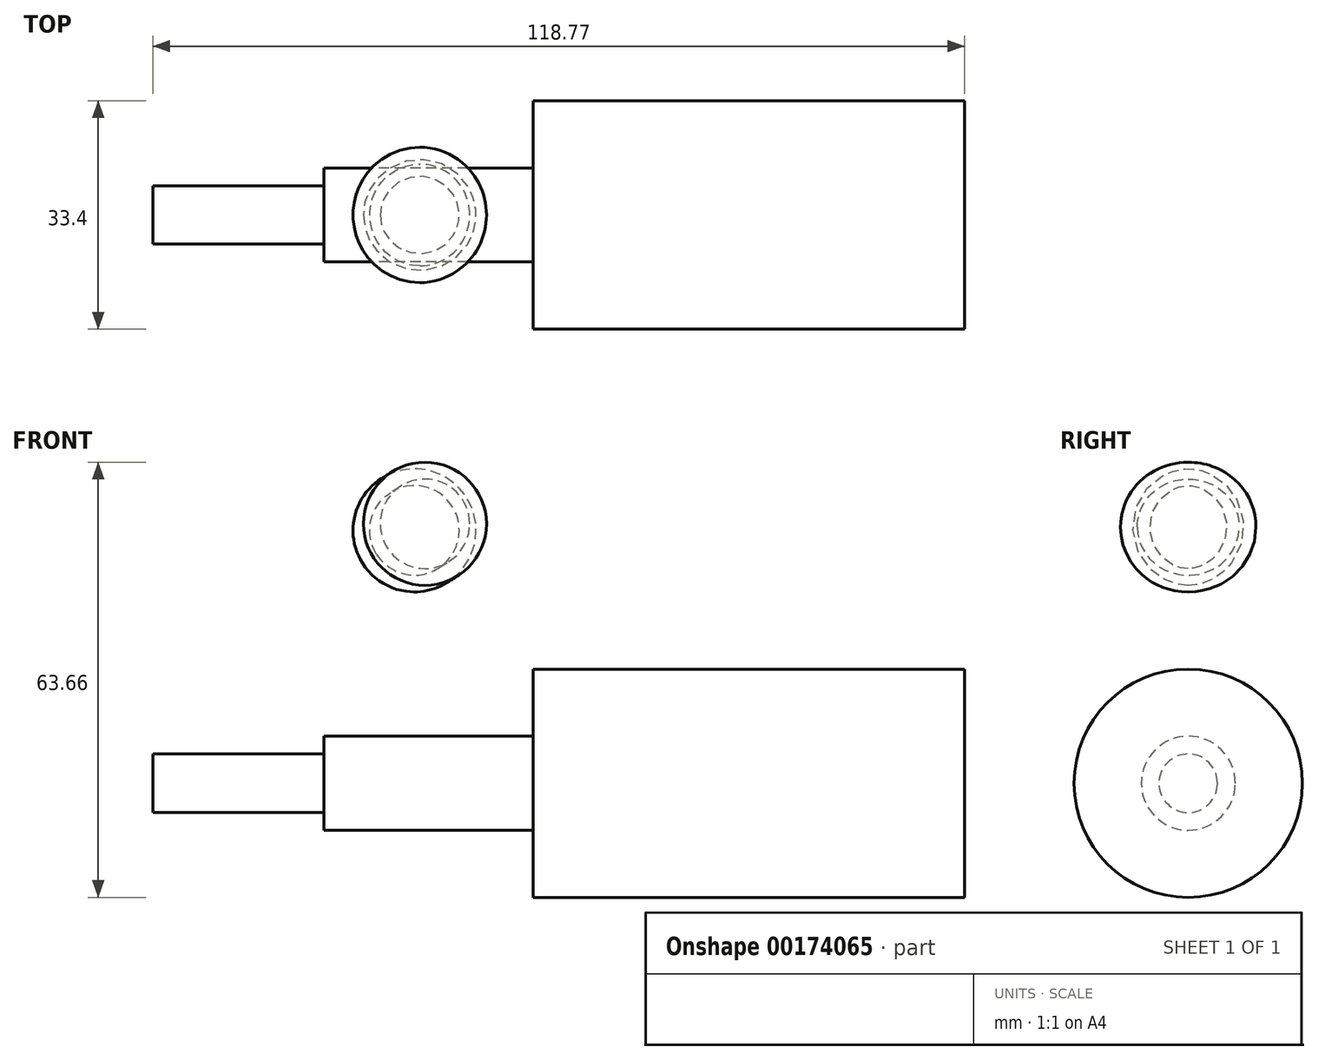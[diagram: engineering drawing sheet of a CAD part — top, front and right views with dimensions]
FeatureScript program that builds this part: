
annotation { "Feature Type Name" : "Feature", "Feature Type Description" : "" }
export const myFeature = defineFeature(function(context is Context, id is Id, definition is map)
    precondition{}
    {
        {
            var Q0;
            Q0=qCreatedBy(makeId("Front.planeOp"),FACE);
            var sketch = newSketch(context, id + "F0", { "sketchPlane" : qUnion([Q0])});
            skLineSegment(sketch, "E0", {"start": v(-42.95, -6.88) * mm, "end": v(-12.35, -6.88) * mm});
            skLineSegment(sketch, "E1", {"start": v(-12.35, -6.88) * mm, "end": v(-12.35, -16.7) * mm});
            skLineSegment(sketch, "E2", {"start": v(-12.35, -16.7) * mm, "end": v(50.82, -16.7) * mm});
            skLineSegment(sketch, "E3", {"start": v(50.82, -16.7) * mm, "end": v(50.82, 0) * mm});
            skLineSegment(sketch, "E4", {"start": v(-42.95, 0) * mm, "end": v(50.82, 0) * mm});
            skLineSegment(sketch, "E5", {"start": v(-42.95, 0) * mm, "end": v(-42.95, -6.88) * mm});
            skSolve(sketch);
        }
        {
            var Q0;
            Q0=makeQuery(id+"F0.imprint","IMPRINT",FACE,{"disambiguationData":[TD([[makeQuery(id+"F0.imprint","IMPRINT",EDGE,{"derivedFrom":sQuery(id+"F0.wireOp",EDGE,"E0")}),1.0]])]});
            var Q1;
            Q1=sQuery(id+"F0.wireOp",EDGE,"E4");
            revolve(context, id + "F1", {"entities" : qUnion([Q0]), "axis" : qUnion([Q1]), "revolveType" : RevolveType.FULL});
        }
        {
            var Q0;
            Q0=qCreatedBy(makeId("Front.planeOp"),FACE);
            var sketch = newSketch(context, id + "F2", { "sketchPlane" : qUnion([Q0])});
            skArc(sketch, "E6", {"start": v(-24.14, 29.9) * mm, "mid": v(-22.06, 41.8) * mm, "end": v(-33.69, 45.06) * mm});
            skLineSegment(sketch, "E7", {"start": v(-33.69, 45.06) * mm, "end": v(-24.14, 29.9) * mm});
            skArc(sketch, "E8", {"start": v(-25.46, 32) * mm, "mid": v(-24.14, 40.49) * mm, "end": v(-32.37, 42.97) * mm});
            skSolve(sketch);
        }
        {
            var Q0;
            {var subQ0=sQuery(id+"F2.wireOp",EDGE,"E6");Q0=makeQuery(id+"F2.imprint","IMPRINT",FACE,{"disambiguationData":[TD([[makeQuery(id+"F2.imprint","IMPRINT",EDGE,{"derivedFrom":subQ0}),1.0]])]});}
            var Q1;
            Q1=sQuery(id+"F2.wireOp",EDGE,"E7");
            revolve(context, id + "F3", {"entities" : qUnion([Q0]), "axis" : qUnion([Q1]), "revolveType" : RevolveType.FULL});
        }
        {
            var Q0;
            Q0=makeQuery(id+"F1.opRevolve","SWEPT_FACE",FACE,{"disambiguationData":[OSD([sQuery(id+"F0.wireOp",EDGE,"E5")])]});
            var sketch = newSketch(context, id + "F4", { "sketchPlane" : qUnion([Q0])});
            skCircle(sketch, "E9", {"center": v(0, 0) * mm, "radius": 4.28 * mm});
            skSolve(sketch);
        }
        {
            var Q0;
            Q0=makeQuery(id+"F4.imprint","IMPRINT",FACE,{"disambiguationData":[TD([[makeQuery(id+"F4.imprint","IMPRINT",EDGE,{"derivedFrom":sQuery(id+"F4.wireOp",EDGE,"E9")}),1.0]])]});
            extrude(context, id + "F5", {"entities" : qUnion([Q0]), "operationType" : NewBodyOperationType.ADD, "depth" : 25 * mm});
        }
    });
